# Revit family: Mixer tap-Wall_mounted-PRESTO-MURAL NEO FROID 65MM 15SEC-66000
name_source: partatom
category: Plumbing Fixtures
revit_build: Autodesk Revit Architecture 2014 (Build: 20130308_1515(x64)
units: mm (PartAtom-declared; Revit-internal decimal feet)

## types (1)
- 66000
    Description = PRESTO NEO Robinet simple temporisé mural (65mm)
    Durée = 7.0 s
    Débit (à 3 bar - régulateur de débit à 4 positions) = 3 l/min à 3 bar
    Edition number = 1
    Entrée EC = 0 mm  [stored 0 ft]
    Entrée EF = 13 mm
    Garantie = 10
    HW Connection = Yes
    Height = 0 mm  [stored 0 ft]
    Lenght = 0 mm  [stored 0 ft]
    Manufacturer = PRESTO LES ROBINETS
    Manufacturer name = Presto
    Material main = Brass
    Material secondary = Chrome
    Matériau Principal = Corps en laiton, conforme aux normes NE 1982, NE 12164, NE 12156
    Matériau Secondare = Corps moulé chromé conforme à la norme NE 12540
    Model = 66000
    Nominal height = 10400
    Nominal width = 0
    Pression de fonctionnement = 1 à 5 bar
    Product Guid = f9d6806c-9562-4352-b354-bb9fc00bde47
    Product SKU = 66000
    Product data url = http://bimobject.com
    Product family = NEO
    Product group = ROBINET
    QR code = http://bimobject.com
    Temp - Résistance (Choc Thermique de 30 Minutes) = 75 °C
    Weight Net (Kg) = 0
    Width = 104 mm

note: [stored X ft] marks values corroborated as IEEE doubles in the binary element streams (Revit-internal decimal feet)

## geometry (parser evidence)
native form markers: Sweep x5
no freeform markers — native parametric forms only
